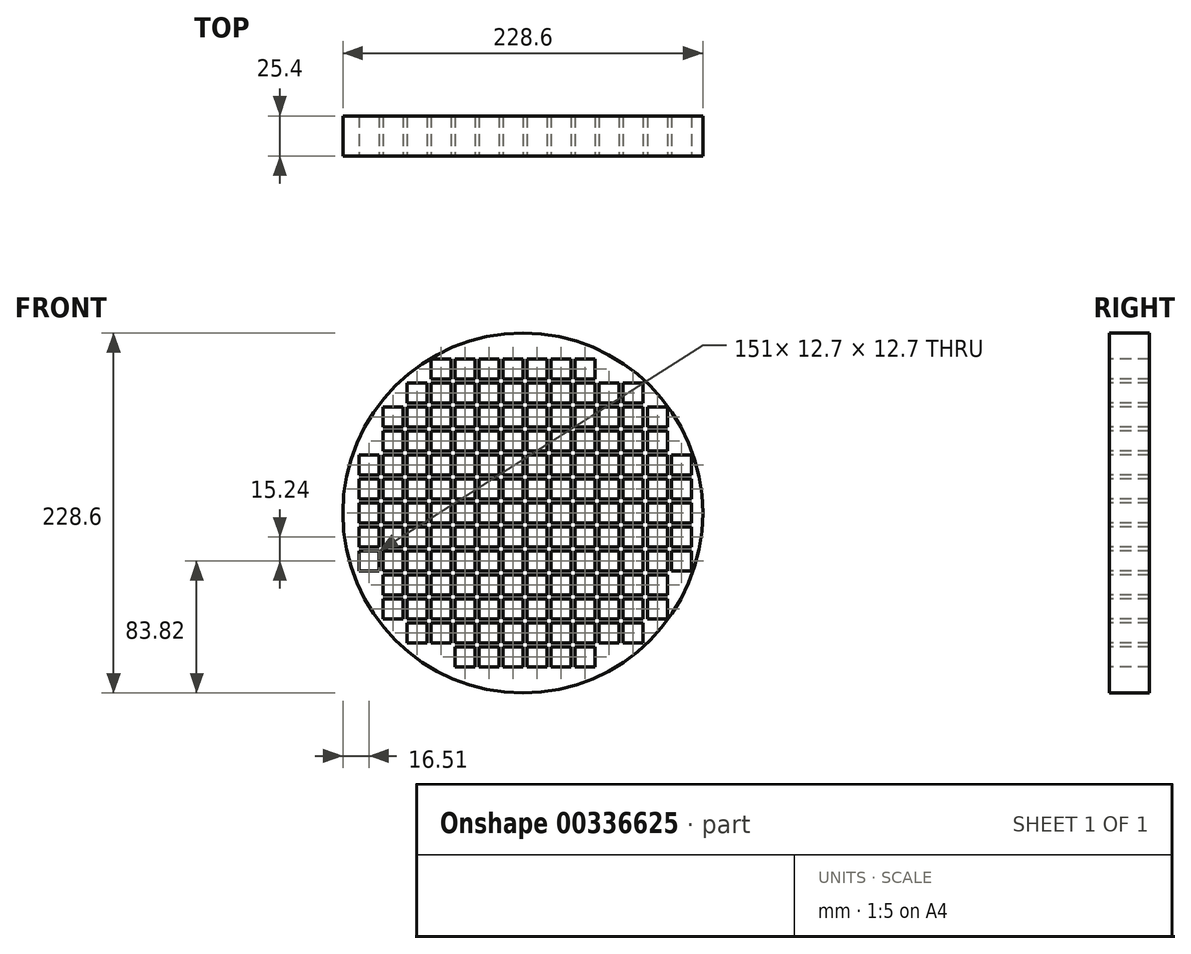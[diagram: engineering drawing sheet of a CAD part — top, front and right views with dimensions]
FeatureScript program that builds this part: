
annotation { "Feature Type Name" : "Feature", "Feature Type Description" : "" }
export const myFeature = defineFeature(function(context is Context, id is Id, definition is map)
    precondition{}
    {
        {
            var Q0;
            Q0=qCreatedBy(makeId("Front.planeOp"),FACE);
            var sketch = newSketch(context, id + "F0", { "sketchPlane" : qUnion([Q0])});
            skCircle(sketch, "E0", {"center": v(0, 0) * mm, "radius": 114.3 * mm});
            skSolve(sketch);
        }
        {
            var Q0;
            Q0 = qSketchRegion(id + "F0", true);
            extrude(context, id + "F1", {"entities" : qUnion([Q0]), "depth" : 25.4 * mm});
        }
        {
            var Q0;
            Q0=makeQuery(id+"F1.opExtrude","CAP_FACE",FACE,{"disambiguationData":[OSD([sQuery(id+"F0.wireOp",EDGE,"E0")])],"isStart":false});
            var sketch = newSketch(context, id + "F2", { "sketchPlane" : qUnion([Q0])});
            skLineSegment(sketch, "E1.bottom", {"start": v(-73.66, 82.55) * mm, "end": v(-60.96, 82.55) * mm});
            skLineSegment(sketch, "E1.top", {"start": v(-73.66, 69.85) * mm, "end": v(-60.96, 69.85) * mm});
            skLineSegment(sketch, "E1.left", {"start": v(-73.66, 82.55) * mm, "end": v(-73.66, 69.85) * mm});
            skLineSegment(sketch, "E1.right", {"start": v(-60.96, 82.55) * mm, "end": v(-60.96, 69.85) * mm});
            skLineSegment(sketch, "E2.0.1.0", {"start": v(-73.66, 67.31) * mm, "end": v(-60.96, 67.31) * mm});
            skLineSegment(sketch, "E2.0.1.1", {"start": v(-73.66, 67.31) * mm, "end": v(-73.66, 54.61) * mm});
            skLineSegment(sketch, "E2.0.1.2", {"start": v(-73.66, 54.61) * mm, "end": v(-60.96, 54.61) * mm});
            skLineSegment(sketch, "E2.0.1.3", {"start": v(-60.96, 67.31) * mm, "end": v(-60.96, 54.61) * mm});
            skLineSegment(sketch, "E2.0.2.0", {"start": v(-73.66, 52.07) * mm, "end": v(-60.96, 52.07) * mm});
            skLineSegment(sketch, "E2.0.2.1", {"start": v(-73.66, 52.07) * mm, "end": v(-73.66, 39.37) * mm});
            skLineSegment(sketch, "E2.0.2.2", {"start": v(-73.66, 39.37) * mm, "end": v(-60.96, 39.37) * mm});
            skLineSegment(sketch, "E2.0.2.3", {"start": v(-60.96, 52.07) * mm, "end": v(-60.96, 39.37) * mm});
            skLineSegment(sketch, "E2.0.3.0", {"start": v(-73.66, 36.83) * mm, "end": v(-60.96, 36.83) * mm});
            skLineSegment(sketch, "E2.0.3.1", {"start": v(-73.66, 36.83) * mm, "end": v(-73.66, 24.13) * mm});
            skLineSegment(sketch, "E2.0.3.2", {"start": v(-73.66, 24.13) * mm, "end": v(-60.96, 24.13) * mm});
            skLineSegment(sketch, "E2.0.3.3", {"start": v(-60.96, 36.83) * mm, "end": v(-60.96, 24.13) * mm});
            skLineSegment(sketch, "E2.0.4.0", {"start": v(-73.66, 21.59) * mm, "end": v(-60.96, 21.59) * mm});
            skLineSegment(sketch, "E2.0.4.1", {"start": v(-73.66, 21.59) * mm, "end": v(-73.66, 8.89) * mm});
            skLineSegment(sketch, "E2.0.4.2", {"start": v(-73.66, 8.89) * mm, "end": v(-60.96, 8.89) * mm});
            skLineSegment(sketch, "E2.0.4.3", {"start": v(-60.96, 21.59) * mm, "end": v(-60.96, 8.89) * mm});
            skLineSegment(sketch, "E2.0.5.0", {"start": v(-73.66, 6.35) * mm, "end": v(-60.96, 6.35) * mm});
            skLineSegment(sketch, "E2.0.5.1", {"start": v(-73.66, 6.35) * mm, "end": v(-73.66, -6.35) * mm});
            skLineSegment(sketch, "E2.0.5.2", {"start": v(-73.66, -6.35) * mm, "end": v(-60.96, -6.35) * mm});
            skLineSegment(sketch, "E2.0.5.3", {"start": v(-60.96, 6.35) * mm, "end": v(-60.96, -6.35) * mm});
            skLineSegment(sketch, "E2.0.6.0", {"start": v(-73.66, -8.9) * mm, "end": v(-60.96, -8.9) * mm});
            skLineSegment(sketch, "E2.0.6.1", {"start": v(-73.66, -8.9) * mm, "end": v(-73.66, -21.6) * mm});
            skLineSegment(sketch, "E2.0.6.2", {"start": v(-73.66, -21.6) * mm, "end": v(-60.96, -21.6) * mm});
            skLineSegment(sketch, "E2.0.6.3", {"start": v(-60.96, -8.9) * mm, "end": v(-60.96, -21.6) * mm});
            skLineSegment(sketch, "E2.0.7.0", {"start": v(-73.66, -24.13) * mm, "end": v(-60.96, -24.13) * mm});
            skLineSegment(sketch, "E2.0.7.1", {"start": v(-73.66, -24.13) * mm, "end": v(-73.66, -36.83) * mm});
            skLineSegment(sketch, "E2.0.7.2", {"start": v(-73.66, -36.83) * mm, "end": v(-60.96, -36.83) * mm});
            skLineSegment(sketch, "E2.0.7.3", {"start": v(-60.96, -24.13) * mm, "end": v(-60.96, -36.83) * mm});
            skLineSegment(sketch, "E2.0.8.0", {"start": v(-73.66, -39.37) * mm, "end": v(-60.96, -39.37) * mm});
            skLineSegment(sketch, "E2.0.8.1", {"start": v(-73.66, -39.37) * mm, "end": v(-73.66, -52.07) * mm});
            skLineSegment(sketch, "E2.0.8.2", {"start": v(-73.66, -52.07) * mm, "end": v(-60.96, -52.07) * mm});
            skLineSegment(sketch, "E2.0.8.3", {"start": v(-60.96, -39.37) * mm, "end": v(-60.96, -52.07) * mm});
            skLineSegment(sketch, "E2.0.9.0", {"start": v(-73.66, -54.61) * mm, "end": v(-60.96, -54.61) * mm});
            skLineSegment(sketch, "E2.0.9.1", {"start": v(-73.66, -54.61) * mm, "end": v(-73.66, -67.31) * mm});
            skLineSegment(sketch, "E2.0.9.2", {"start": v(-73.66, -67.31) * mm, "end": v(-60.96, -67.31) * mm});
            skLineSegment(sketch, "E2.0.9.3", {"start": v(-60.96, -54.61) * mm, "end": v(-60.96, -67.31) * mm});
            skLineSegment(sketch, "E2.1.0.0", {"start": v(-58.42, 82.55) * mm, "end": v(-45.72, 82.55) * mm});
            skLineSegment(sketch, "E2.1.0.1", {"start": v(-58.42, 82.55) * mm, "end": v(-58.42, 69.85) * mm});
            skLineSegment(sketch, "E2.1.0.2", {"start": v(-58.42, 69.85) * mm, "end": v(-45.72, 69.85) * mm});
            skLineSegment(sketch, "E2.1.0.3", {"start": v(-45.72, 82.55) * mm, "end": v(-45.72, 69.85) * mm});
            skLineSegment(sketch, "E2.1.1.0", {"start": v(-58.42, 67.31) * mm, "end": v(-45.72, 67.31) * mm});
            skLineSegment(sketch, "E2.1.1.1", {"start": v(-58.42, 67.31) * mm, "end": v(-58.42, 54.61) * mm});
            skLineSegment(sketch, "E2.1.1.2", {"start": v(-58.42, 54.61) * mm, "end": v(-45.72, 54.61) * mm});
            skLineSegment(sketch, "E2.1.1.3", {"start": v(-45.72, 67.31) * mm, "end": v(-45.72, 54.61) * mm});
            skLineSegment(sketch, "E2.1.2.0", {"start": v(-58.42, 52.07) * mm, "end": v(-45.72, 52.07) * mm});
            skLineSegment(sketch, "E2.1.2.1", {"start": v(-58.42, 52.07) * mm, "end": v(-58.42, 39.37) * mm});
            skLineSegment(sketch, "E2.1.2.2", {"start": v(-58.42, 39.37) * mm, "end": v(-45.72, 39.37) * mm});
            skLineSegment(sketch, "E2.1.2.3", {"start": v(-45.72, 52.07) * mm, "end": v(-45.72, 39.37) * mm});
            skLineSegment(sketch, "E2.1.3.0", {"start": v(-58.42, 36.83) * mm, "end": v(-45.72, 36.83) * mm});
            skLineSegment(sketch, "E2.1.3.1", {"start": v(-58.42, 36.83) * mm, "end": v(-58.42, 24.13) * mm});
            skLineSegment(sketch, "E2.1.3.2", {"start": v(-58.42, 24.13) * mm, "end": v(-45.72, 24.13) * mm});
            skLineSegment(sketch, "E2.1.3.3", {"start": v(-45.72, 36.83) * mm, "end": v(-45.72, 24.13) * mm});
            skLineSegment(sketch, "E2.1.4.0", {"start": v(-58.42, 21.59) * mm, "end": v(-45.72, 21.59) * mm});
            skLineSegment(sketch, "E2.1.4.1", {"start": v(-58.42, 21.59) * mm, "end": v(-58.42, 8.89) * mm});
            skLineSegment(sketch, "E2.1.4.2", {"start": v(-58.42, 8.89) * mm, "end": v(-45.72, 8.89) * mm});
            skLineSegment(sketch, "E2.1.4.3", {"start": v(-45.72, 21.59) * mm, "end": v(-45.72, 8.89) * mm});
            skLineSegment(sketch, "E2.1.5.0", {"start": v(-58.42, 6.35) * mm, "end": v(-45.72, 6.35) * mm});
            skLineSegment(sketch, "E2.1.5.1", {"start": v(-58.42, 6.35) * mm, "end": v(-58.42, -6.35) * mm});
            skLineSegment(sketch, "E2.1.5.2", {"start": v(-58.42, -6.35) * mm, "end": v(-45.72, -6.35) * mm});
            skLineSegment(sketch, "E2.1.5.3", {"start": v(-45.72, 6.35) * mm, "end": v(-45.72, -6.35) * mm});
            skLineSegment(sketch, "E2.1.6.0", {"start": v(-58.42, -8.9) * mm, "end": v(-45.72, -8.9) * mm});
            skLineSegment(sketch, "E2.1.6.1", {"start": v(-58.42, -8.9) * mm, "end": v(-58.42, -21.6) * mm});
            skLineSegment(sketch, "E2.1.6.2", {"start": v(-58.42, -21.6) * mm, "end": v(-45.72, -21.6) * mm});
            skLineSegment(sketch, "E2.1.6.3", {"start": v(-45.72, -8.9) * mm, "end": v(-45.72, -21.6) * mm});
            skLineSegment(sketch, "E2.1.7.0", {"start": v(-58.42, -24.13) * mm, "end": v(-45.72, -24.13) * mm});
            skLineSegment(sketch, "E2.1.7.1", {"start": v(-58.42, -24.13) * mm, "end": v(-58.42, -36.83) * mm});
            skLineSegment(sketch, "E2.1.7.2", {"start": v(-58.42, -36.83) * mm, "end": v(-45.72, -36.83) * mm});
            skLineSegment(sketch, "E2.1.7.3", {"start": v(-45.72, -24.13) * mm, "end": v(-45.72, -36.83) * mm});
            skLineSegment(sketch, "E2.1.8.0", {"start": v(-58.42, -39.37) * mm, "end": v(-45.72, -39.37) * mm});
            skLineSegment(sketch, "E2.1.8.1", {"start": v(-58.42, -39.37) * mm, "end": v(-58.42, -52.07) * mm});
            skLineSegment(sketch, "E2.1.8.2", {"start": v(-58.42, -52.07) * mm, "end": v(-45.72, -52.07) * mm});
            skLineSegment(sketch, "E2.1.8.3", {"start": v(-45.72, -39.37) * mm, "end": v(-45.72, -52.07) * mm});
            skLineSegment(sketch, "E2.1.9.0", {"start": v(-58.42, -54.61) * mm, "end": v(-45.72, -54.61) * mm});
            skLineSegment(sketch, "E2.1.9.1", {"start": v(-58.42, -54.61) * mm, "end": v(-58.42, -67.31) * mm});
            skLineSegment(sketch, "E2.1.9.2", {"start": v(-58.42, -67.31) * mm, "end": v(-45.72, -67.31) * mm});
            skLineSegment(sketch, "E2.1.9.3", {"start": v(-45.72, -54.61) * mm, "end": v(-45.72, -67.31) * mm});
            skLineSegment(sketch, "E2.2.0.0", {"start": v(-43.18, 82.55) * mm, "end": v(-30.48, 82.55) * mm});
            skLineSegment(sketch, "E2.2.0.1", {"start": v(-43.18, 82.55) * mm, "end": v(-43.18, 69.85) * mm});
            skLineSegment(sketch, "E2.2.0.2", {"start": v(-43.18, 69.85) * mm, "end": v(-30.48, 69.85) * mm});
            skLineSegment(sketch, "E2.2.0.3", {"start": v(-30.48, 82.55) * mm, "end": v(-30.48, 69.85) * mm});
            skLineSegment(sketch, "E2.2.1.0", {"start": v(-43.18, 67.31) * mm, "end": v(-30.48, 67.31) * mm});
            skLineSegment(sketch, "E2.2.1.1", {"start": v(-43.18, 67.31) * mm, "end": v(-43.18, 54.61) * mm});
            skLineSegment(sketch, "E2.2.1.2", {"start": v(-43.18, 54.61) * mm, "end": v(-30.48, 54.61) * mm});
            skLineSegment(sketch, "E2.2.1.3", {"start": v(-30.48, 67.31) * mm, "end": v(-30.48, 54.61) * mm});
            skLineSegment(sketch, "E2.2.2.0", {"start": v(-43.18, 52.07) * mm, "end": v(-30.48, 52.07) * mm});
            skLineSegment(sketch, "E2.2.2.1", {"start": v(-43.18, 52.07) * mm, "end": v(-43.18, 39.37) * mm});
            skLineSegment(sketch, "E2.2.2.2", {"start": v(-43.18, 39.37) * mm, "end": v(-30.48, 39.37) * mm});
            skLineSegment(sketch, "E2.2.2.3", {"start": v(-30.48, 52.07) * mm, "end": v(-30.48, 39.37) * mm});
            skLineSegment(sketch, "E2.2.3.0", {"start": v(-43.18, 36.83) * mm, "end": v(-30.48, 36.83) * mm});
            skLineSegment(sketch, "E2.2.3.1", {"start": v(-43.18, 36.83) * mm, "end": v(-43.18, 24.13) * mm});
            skLineSegment(sketch, "E2.2.3.2", {"start": v(-43.18, 24.13) * mm, "end": v(-30.48, 24.13) * mm});
            skLineSegment(sketch, "E2.2.3.3", {"start": v(-30.48, 36.83) * mm, "end": v(-30.48, 24.13) * mm});
            skLineSegment(sketch, "E2.2.4.0", {"start": v(-43.18, 21.59) * mm, "end": v(-30.48, 21.59) * mm});
            skLineSegment(sketch, "E2.2.4.1", {"start": v(-43.18, 21.59) * mm, "end": v(-43.18, 8.89) * mm});
            skLineSegment(sketch, "E2.2.4.2", {"start": v(-43.18, 8.89) * mm, "end": v(-30.48, 8.89) * mm});
            skLineSegment(sketch, "E2.2.4.3", {"start": v(-30.48, 21.59) * mm, "end": v(-30.48, 8.89) * mm});
            skLineSegment(sketch, "E2.2.5.0", {"start": v(-43.18, 6.35) * mm, "end": v(-30.48, 6.35) * mm});
            skLineSegment(sketch, "E2.2.5.1", {"start": v(-43.18, 6.35) * mm, "end": v(-43.18, -6.35) * mm});
            skLineSegment(sketch, "E2.2.5.2", {"start": v(-43.18, -6.35) * mm, "end": v(-30.48, -6.35) * mm});
            skLineSegment(sketch, "E2.2.5.3", {"start": v(-30.48, 6.35) * mm, "end": v(-30.48, -6.35) * mm});
            skLineSegment(sketch, "E2.2.6.0", {"start": v(-43.18, -8.9) * mm, "end": v(-30.48, -8.9) * mm});
            skLineSegment(sketch, "E2.2.6.1", {"start": v(-43.18, -8.9) * mm, "end": v(-43.18, -21.6) * mm});
            skLineSegment(sketch, "E2.2.6.2", {"start": v(-43.18, -21.6) * mm, "end": v(-30.48, -21.6) * mm});
            skLineSegment(sketch, "E2.2.6.3", {"start": v(-30.48, -8.9) * mm, "end": v(-30.48, -21.6) * mm});
            skLineSegment(sketch, "E2.2.7.0", {"start": v(-43.18, -24.13) * mm, "end": v(-30.48, -24.13) * mm});
            skLineSegment(sketch, "E2.2.7.1", {"start": v(-43.18, -24.13) * mm, "end": v(-43.18, -36.83) * mm});
            skLineSegment(sketch, "E2.2.7.2", {"start": v(-43.18, -36.83) * mm, "end": v(-30.48, -36.83) * mm});
            skLineSegment(sketch, "E2.2.7.3", {"start": v(-30.48, -24.13) * mm, "end": v(-30.48, -36.83) * mm});
            skLineSegment(sketch, "E2.2.8.0", {"start": v(-43.18, -39.37) * mm, "end": v(-30.48, -39.37) * mm});
            skLineSegment(sketch, "E2.2.8.1", {"start": v(-43.18, -39.37) * mm, "end": v(-43.18, -52.07) * mm});
            skLineSegment(sketch, "E2.2.8.2", {"start": v(-43.18, -52.07) * mm, "end": v(-30.48, -52.07) * mm});
            skLineSegment(sketch, "E2.2.8.3", {"start": v(-30.48, -39.37) * mm, "end": v(-30.48, -52.07) * mm});
            skLineSegment(sketch, "E2.2.9.0", {"start": v(-43.18, -54.61) * mm, "end": v(-30.48, -54.61) * mm});
            skLineSegment(sketch, "E2.2.9.1", {"start": v(-43.18, -54.61) * mm, "end": v(-43.18, -67.31) * mm});
            skLineSegment(sketch, "E2.2.9.2", {"start": v(-43.18, -67.31) * mm, "end": v(-30.48, -67.31) * mm});
            skLineSegment(sketch, "E2.2.9.3", {"start": v(-30.48, -54.61) * mm, "end": v(-30.48, -67.31) * mm});
            skLineSegment(sketch, "E2.3.0.0", {"start": v(-27.94, 82.55) * mm, "end": v(-15.24, 82.55) * mm});
            skLineSegment(sketch, "E2.3.0.1", {"start": v(-27.94, 82.55) * mm, "end": v(-27.94, 69.85) * mm});
            skLineSegment(sketch, "E2.3.0.2", {"start": v(-27.94, 69.85) * mm, "end": v(-15.24, 69.85) * mm});
            skLineSegment(sketch, "E2.3.0.3", {"start": v(-15.24, 82.55) * mm, "end": v(-15.24, 69.85) * mm});
            skLineSegment(sketch, "E2.3.1.0", {"start": v(-27.94, 67.31) * mm, "end": v(-15.24, 67.31) * mm});
            skLineSegment(sketch, "E2.3.1.1", {"start": v(-27.94, 67.31) * mm, "end": v(-27.94, 54.61) * mm});
            skLineSegment(sketch, "E2.3.1.2", {"start": v(-27.94, 54.61) * mm, "end": v(-15.24, 54.61) * mm});
            skLineSegment(sketch, "E2.3.1.3", {"start": v(-15.24, 67.31) * mm, "end": v(-15.24, 54.61) * mm});
            skLineSegment(sketch, "E2.3.2.0", {"start": v(-27.94, 52.07) * mm, "end": v(-15.24, 52.07) * mm});
            skLineSegment(sketch, "E2.3.2.1", {"start": v(-27.94, 52.07) * mm, "end": v(-27.94, 39.37) * mm});
            skLineSegment(sketch, "E2.3.2.2", {"start": v(-27.94, 39.37) * mm, "end": v(-15.24, 39.37) * mm});
            skLineSegment(sketch, "E2.3.2.3", {"start": v(-15.24, 52.07) * mm, "end": v(-15.24, 39.37) * mm});
            skLineSegment(sketch, "E2.3.3.0", {"start": v(-27.94, 36.83) * mm, "end": v(-15.24, 36.83) * mm});
            skLineSegment(sketch, "E2.3.3.1", {"start": v(-27.94, 36.83) * mm, "end": v(-27.94, 24.13) * mm});
            skLineSegment(sketch, "E2.3.3.2", {"start": v(-27.94, 24.13) * mm, "end": v(-15.24, 24.13) * mm});
            skLineSegment(sketch, "E2.3.3.3", {"start": v(-15.24, 36.83) * mm, "end": v(-15.24, 24.13) * mm});
            skLineSegment(sketch, "E2.3.4.0", {"start": v(-27.94, 21.59) * mm, "end": v(-15.24, 21.59) * mm});
            skLineSegment(sketch, "E2.3.4.1", {"start": v(-27.94, 21.59) * mm, "end": v(-27.94, 8.89) * mm});
            skLineSegment(sketch, "E2.3.4.2", {"start": v(-27.94, 8.89) * mm, "end": v(-15.24, 8.89) * mm});
            skLineSegment(sketch, "E2.3.4.3", {"start": v(-15.24, 21.59) * mm, "end": v(-15.24, 8.89) * mm});
            skLineSegment(sketch, "E2.3.5.0", {"start": v(-27.94, 6.35) * mm, "end": v(-15.24, 6.35) * mm});
            skLineSegment(sketch, "E2.3.5.1", {"start": v(-27.94, 6.35) * mm, "end": v(-27.94, -6.35) * mm});
            skLineSegment(sketch, "E2.3.5.2", {"start": v(-27.94, -6.35) * mm, "end": v(-15.24, -6.35) * mm});
            skLineSegment(sketch, "E2.3.5.3", {"start": v(-15.24, 6.35) * mm, "end": v(-15.24, -6.35) * mm});
            skLineSegment(sketch, "E2.3.6.0", {"start": v(-27.94, -8.9) * mm, "end": v(-15.24, -8.9) * mm});
            skLineSegment(sketch, "E2.3.6.1", {"start": v(-27.94, -8.9) * mm, "end": v(-27.94, -21.6) * mm});
            skLineSegment(sketch, "E2.3.6.2", {"start": v(-27.94, -21.6) * mm, "end": v(-15.24, -21.6) * mm});
            skLineSegment(sketch, "E2.3.6.3", {"start": v(-15.24, -8.9) * mm, "end": v(-15.24, -21.6) * mm});
            skLineSegment(sketch, "E2.3.7.0", {"start": v(-27.94, -24.13) * mm, "end": v(-15.24, -24.13) * mm});
            skLineSegment(sketch, "E2.3.7.1", {"start": v(-27.94, -24.13) * mm, "end": v(-27.94, -36.83) * mm});
            skLineSegment(sketch, "E2.3.7.2", {"start": v(-27.94, -36.83) * mm, "end": v(-15.24, -36.83) * mm});
            skLineSegment(sketch, "E2.3.7.3", {"start": v(-15.24, -24.13) * mm, "end": v(-15.24, -36.83) * mm});
            skLineSegment(sketch, "E2.3.8.0", {"start": v(-27.94, -39.37) * mm, "end": v(-15.24, -39.37) * mm});
            skLineSegment(sketch, "E2.3.8.1", {"start": v(-27.94, -39.37) * mm, "end": v(-27.94, -52.07) * mm});
            skLineSegment(sketch, "E2.3.8.2", {"start": v(-27.94, -52.07) * mm, "end": v(-15.24, -52.07) * mm});
            skLineSegment(sketch, "E2.3.8.3", {"start": v(-15.24, -39.37) * mm, "end": v(-15.24, -52.07) * mm});
            skLineSegment(sketch, "E2.3.9.0", {"start": v(-27.94, -54.61) * mm, "end": v(-15.24, -54.61) * mm});
            skLineSegment(sketch, "E2.3.9.1", {"start": v(-27.94, -54.61) * mm, "end": v(-27.94, -67.31) * mm});
            skLineSegment(sketch, "E2.3.9.2", {"start": v(-27.94, -67.31) * mm, "end": v(-15.24, -67.31) * mm});
            skLineSegment(sketch, "E2.3.9.3", {"start": v(-15.24, -54.61) * mm, "end": v(-15.24, -67.31) * mm});
            skLineSegment(sketch, "E2.4.0.0", {"start": v(-12.7, 82.55) * mm, "end": v(0, 82.55) * mm});
            skLineSegment(sketch, "E2.4.0.1", {"start": v(-12.7, 82.55) * mm, "end": v(-12.7, 69.85) * mm});
            skLineSegment(sketch, "E2.4.0.2", {"start": v(-12.7, 69.85) * mm, "end": v(0, 69.85) * mm});
            skLineSegment(sketch, "E2.4.0.3", {"start": v(0, 82.55) * mm, "end": v(0, 69.85) * mm});
            skLineSegment(sketch, "E2.4.1.0", {"start": v(-12.7, 67.31) * mm, "end": v(0, 67.31) * mm});
            skLineSegment(sketch, "E2.4.1.1", {"start": v(-12.7, 67.31) * mm, "end": v(-12.7, 54.61) * mm});
            skLineSegment(sketch, "E2.4.1.2", {"start": v(-12.7, 54.61) * mm, "end": v(0, 54.61) * mm});
            skLineSegment(sketch, "E2.4.1.3", {"start": v(0, 67.31) * mm, "end": v(0, 54.61) * mm});
            skLineSegment(sketch, "E2.4.2.0", {"start": v(-12.7, 52.07) * mm, "end": v(0, 52.07) * mm});
            skLineSegment(sketch, "E2.4.2.1", {"start": v(-12.7, 52.07) * mm, "end": v(-12.7, 39.37) * mm});
            skLineSegment(sketch, "E2.4.2.2", {"start": v(-12.7, 39.37) * mm, "end": v(0, 39.37) * mm});
            skLineSegment(sketch, "E2.4.2.3", {"start": v(0, 52.07) * mm, "end": v(0, 39.37) * mm});
            skLineSegment(sketch, "E2.4.3.0", {"start": v(-12.7, 36.83) * mm, "end": v(0, 36.83) * mm});
            skLineSegment(sketch, "E2.4.3.1", {"start": v(-12.7, 36.83) * mm, "end": v(-12.7, 24.13) * mm});
            skLineSegment(sketch, "E2.4.3.2", {"start": v(-12.7, 24.13) * mm, "end": v(0, 24.13) * mm});
            skLineSegment(sketch, "E2.4.3.3", {"start": v(0, 36.83) * mm, "end": v(0, 24.13) * mm});
            skLineSegment(sketch, "E2.4.4.0", {"start": v(-12.7, 21.59) * mm, "end": v(0, 21.59) * mm});
            skLineSegment(sketch, "E2.4.4.1", {"start": v(-12.7, 21.59) * mm, "end": v(-12.7, 8.89) * mm});
            skLineSegment(sketch, "E2.4.4.2", {"start": v(-12.7, 8.89) * mm, "end": v(0, 8.89) * mm});
            skLineSegment(sketch, "E2.4.4.3", {"start": v(0, 21.59) * mm, "end": v(0, 8.89) * mm});
            skLineSegment(sketch, "E2.4.5.0", {"start": v(-12.7, 6.35) * mm, "end": v(0, 6.35) * mm});
            skLineSegment(sketch, "E2.4.5.1", {"start": v(-12.7, 6.35) * mm, "end": v(-12.7, -6.35) * mm});
            skLineSegment(sketch, "E2.4.5.2", {"start": v(-12.7, -6.35) * mm, "end": v(0, -6.35) * mm});
            skLineSegment(sketch, "E2.4.5.3", {"start": v(0, 6.35) * mm, "end": v(0, -6.35) * mm});
            skLineSegment(sketch, "E2.4.6.0", {"start": v(-12.7, -8.9) * mm, "end": v(0, -8.9) * mm});
            skLineSegment(sketch, "E2.4.6.1", {"start": v(-12.7, -8.9) * mm, "end": v(-12.7, -21.6) * mm});
            skLineSegment(sketch, "E2.4.6.2", {"start": v(-12.7, -21.6) * mm, "end": v(0, -21.6) * mm});
            skLineSegment(sketch, "E2.4.6.3", {"start": v(0, -8.9) * mm, "end": v(0, -21.6) * mm});
            skLineSegment(sketch, "E2.4.7.0", {"start": v(-12.7, -24.13) * mm, "end": v(0, -24.13) * mm});
            skLineSegment(sketch, "E2.4.7.1", {"start": v(-12.7, -24.13) * mm, "end": v(-12.7, -36.83) * mm});
            skLineSegment(sketch, "E2.4.7.2", {"start": v(-12.7, -36.83) * mm, "end": v(0, -36.83) * mm});
            skLineSegment(sketch, "E2.4.7.3", {"start": v(0, -24.13) * mm, "end": v(0, -36.83) * mm});
            skLineSegment(sketch, "E2.4.8.0", {"start": v(-12.7, -39.37) * mm, "end": v(0, -39.37) * mm});
            skLineSegment(sketch, "E2.4.8.1", {"start": v(-12.7, -39.37) * mm, "end": v(-12.7, -52.07) * mm});
            skLineSegment(sketch, "E2.4.8.2", {"start": v(-12.7, -52.07) * mm, "end": v(0, -52.07) * mm});
            skLineSegment(sketch, "E2.4.8.3", {"start": v(0, -39.37) * mm, "end": v(0, -52.07) * mm});
            skLineSegment(sketch, "E2.4.9.0", {"start": v(-12.7, -54.61) * mm, "end": v(0, -54.61) * mm});
            skLineSegment(sketch, "E2.4.9.1", {"start": v(-12.7, -54.61) * mm, "end": v(-12.7, -67.31) * mm});
            skLineSegment(sketch, "E2.4.9.2", {"start": v(-12.7, -67.31) * mm, "end": v(0, -67.31) * mm});
            skLineSegment(sketch, "E2.4.9.3", {"start": v(0, -54.61) * mm, "end": v(0, -67.31) * mm});
            skLineSegment(sketch, "E2.5.0.0", {"start": v(2.54, 82.55) * mm, "end": v(15.24, 82.55) * mm});
            skLineSegment(sketch, "E2.5.0.1", {"start": v(2.54, 82.55) * mm, "end": v(2.54, 69.85) * mm});
            skLineSegment(sketch, "E2.5.0.2", {"start": v(2.54, 69.85) * mm, "end": v(15.24, 69.85) * mm});
            skLineSegment(sketch, "E2.5.0.3", {"start": v(15.24, 82.55) * mm, "end": v(15.24, 69.85) * mm});
            skLineSegment(sketch, "E2.5.1.0", {"start": v(2.54, 67.31) * mm, "end": v(15.24, 67.31) * mm});
            skLineSegment(sketch, "E2.5.1.1", {"start": v(2.54, 67.31) * mm, "end": v(2.54, 54.61) * mm});
            skLineSegment(sketch, "E2.5.1.2", {"start": v(2.54, 54.61) * mm, "end": v(15.24, 54.61) * mm});
            skLineSegment(sketch, "E2.5.1.3", {"start": v(15.24, 67.31) * mm, "end": v(15.24, 54.61) * mm});
            skLineSegment(sketch, "E2.5.2.0", {"start": v(2.54, 52.07) * mm, "end": v(15.24, 52.07) * mm});
            skLineSegment(sketch, "E2.5.2.1", {"start": v(2.54, 52.07) * mm, "end": v(2.54, 39.37) * mm});
            skLineSegment(sketch, "E2.5.2.2", {"start": v(2.54, 39.37) * mm, "end": v(15.24, 39.37) * mm});
            skLineSegment(sketch, "E2.5.2.3", {"start": v(15.24, 52.07) * mm, "end": v(15.24, 39.37) * mm});
            skLineSegment(sketch, "E2.5.3.0", {"start": v(2.54, 36.83) * mm, "end": v(15.24, 36.83) * mm});
            skLineSegment(sketch, "E2.5.3.1", {"start": v(2.54, 36.83) * mm, "end": v(2.54, 24.13) * mm});
            skLineSegment(sketch, "E2.5.3.2", {"start": v(2.54, 24.13) * mm, "end": v(15.24, 24.13) * mm});
            skLineSegment(sketch, "E2.5.3.3", {"start": v(15.24, 36.83) * mm, "end": v(15.24, 24.13) * mm});
            skLineSegment(sketch, "E2.5.4.0", {"start": v(2.54, 21.59) * mm, "end": v(15.24, 21.59) * mm});
            skLineSegment(sketch, "E2.5.4.1", {"start": v(2.54, 21.59) * mm, "end": v(2.54, 8.89) * mm});
            skLineSegment(sketch, "E2.5.4.2", {"start": v(2.54, 8.89) * mm, "end": v(15.24, 8.89) * mm});
            skLineSegment(sketch, "E2.5.4.3", {"start": v(15.24, 21.59) * mm, "end": v(15.24, 8.89) * mm});
            skLineSegment(sketch, "E2.5.5.0", {"start": v(2.54, 6.35) * mm, "end": v(15.24, 6.35) * mm});
            skLineSegment(sketch, "E2.5.5.1", {"start": v(2.54, 6.35) * mm, "end": v(2.54, -6.35) * mm});
            skLineSegment(sketch, "E2.5.5.2", {"start": v(2.54, -6.35) * mm, "end": v(15.24, -6.35) * mm});
            skLineSegment(sketch, "E2.5.5.3", {"start": v(15.24, 6.35) * mm, "end": v(15.24, -6.35) * mm});
            skLineSegment(sketch, "E2.5.6.0", {"start": v(2.54, -8.9) * mm, "end": v(15.24, -8.9) * mm});
            skLineSegment(sketch, "E2.5.6.1", {"start": v(2.54, -8.9) * mm, "end": v(2.54, -21.6) * mm});
            skLineSegment(sketch, "E2.5.6.2", {"start": v(2.54, -21.6) * mm, "end": v(15.24, -21.6) * mm});
            skLineSegment(sketch, "E2.5.6.3", {"start": v(15.24, -8.9) * mm, "end": v(15.24, -21.6) * mm});
            skLineSegment(sketch, "E2.5.7.0", {"start": v(2.54, -24.13) * mm, "end": v(15.24, -24.13) * mm});
            skLineSegment(sketch, "E2.5.7.1", {"start": v(2.54, -24.13) * mm, "end": v(2.54, -36.83) * mm});
            skLineSegment(sketch, "E2.5.7.2", {"start": v(2.54, -36.83) * mm, "end": v(15.24, -36.83) * mm});
            skLineSegment(sketch, "E2.5.7.3", {"start": v(15.24, -24.13) * mm, "end": v(15.24, -36.83) * mm});
            skLineSegment(sketch, "E2.5.8.0", {"start": v(2.54, -39.37) * mm, "end": v(15.24, -39.37) * mm});
            skLineSegment(sketch, "E2.5.8.1", {"start": v(2.54, -39.37) * mm, "end": v(2.54, -52.07) * mm});
            skLineSegment(sketch, "E2.5.8.2", {"start": v(2.54, -52.07) * mm, "end": v(15.24, -52.07) * mm});
            skLineSegment(sketch, "E2.5.8.3", {"start": v(15.24, -39.37) * mm, "end": v(15.24, -52.07) * mm});
            skLineSegment(sketch, "E2.5.9.0", {"start": v(2.54, -54.61) * mm, "end": v(15.24, -54.61) * mm});
            skLineSegment(sketch, "E2.5.9.1", {"start": v(2.54, -54.61) * mm, "end": v(2.54, -67.31) * mm});
            skLineSegment(sketch, "E2.5.9.2", {"start": v(2.54, -67.31) * mm, "end": v(15.24, -67.31) * mm});
            skLineSegment(sketch, "E2.5.9.3", {"start": v(15.24, -54.61) * mm, "end": v(15.24, -67.31) * mm});
            skLineSegment(sketch, "E2.6.0.0", {"start": v(17.78, 82.55) * mm, "end": v(30.48, 82.55) * mm});
            skLineSegment(sketch, "E2.6.0.1", {"start": v(17.78, 82.55) * mm, "end": v(17.78, 69.85) * mm});
            skLineSegment(sketch, "E2.6.0.2", {"start": v(17.78, 69.85) * mm, "end": v(30.48, 69.85) * mm});
            skLineSegment(sketch, "E2.6.0.3", {"start": v(30.48, 82.55) * mm, "end": v(30.48, 69.85) * mm});
            skLineSegment(sketch, "E2.6.1.0", {"start": v(17.78, 67.31) * mm, "end": v(30.48, 67.31) * mm});
            skLineSegment(sketch, "E2.6.1.1", {"start": v(17.78, 67.31) * mm, "end": v(17.78, 54.61) * mm});
            skLineSegment(sketch, "E2.6.1.2", {"start": v(17.78, 54.61) * mm, "end": v(30.48, 54.61) * mm});
            skLineSegment(sketch, "E2.6.1.3", {"start": v(30.48, 67.31) * mm, "end": v(30.48, 54.61) * mm});
            skLineSegment(sketch, "E2.6.2.0", {"start": v(17.78, 52.07) * mm, "end": v(30.48, 52.07) * mm});
            skLineSegment(sketch, "E2.6.2.1", {"start": v(17.78, 52.07) * mm, "end": v(17.78, 39.37) * mm});
            skLineSegment(sketch, "E2.6.2.2", {"start": v(17.78, 39.37) * mm, "end": v(30.48, 39.37) * mm});
            skLineSegment(sketch, "E2.6.2.3", {"start": v(30.48, 52.07) * mm, "end": v(30.48, 39.37) * mm});
            skLineSegment(sketch, "E2.6.3.0", {"start": v(17.78, 36.83) * mm, "end": v(30.48, 36.83) * mm});
            skLineSegment(sketch, "E2.6.3.1", {"start": v(17.78, 36.83) * mm, "end": v(17.78, 24.13) * mm});
            skLineSegment(sketch, "E2.6.3.2", {"start": v(17.78, 24.13) * mm, "end": v(30.48, 24.13) * mm});
            skLineSegment(sketch, "E2.6.3.3", {"start": v(30.48, 36.83) * mm, "end": v(30.48, 24.13) * mm});
            skLineSegment(sketch, "E2.6.4.0", {"start": v(17.78, 21.59) * mm, "end": v(30.48, 21.59) * mm});
            skLineSegment(sketch, "E2.6.4.1", {"start": v(17.78, 21.59) * mm, "end": v(17.78, 8.89) * mm});
            skLineSegment(sketch, "E2.6.4.2", {"start": v(17.78, 8.89) * mm, "end": v(30.48, 8.89) * mm});
            skLineSegment(sketch, "E2.6.4.3", {"start": v(30.48, 21.59) * mm, "end": v(30.48, 8.89) * mm});
            skLineSegment(sketch, "E2.6.5.0", {"start": v(17.78, 6.35) * mm, "end": v(30.48, 6.35) * mm});
            skLineSegment(sketch, "E2.6.5.1", {"start": v(17.78, 6.35) * mm, "end": v(17.78, -6.35) * mm});
            skLineSegment(sketch, "E2.6.5.2", {"start": v(17.78, -6.35) * mm, "end": v(30.48, -6.35) * mm});
            skLineSegment(sketch, "E2.6.5.3", {"start": v(30.48, 6.35) * mm, "end": v(30.48, -6.35) * mm});
            skLineSegment(sketch, "E2.6.6.0", {"start": v(17.78, -8.9) * mm, "end": v(30.48, -8.9) * mm});
            skLineSegment(sketch, "E2.6.6.1", {"start": v(17.78, -8.9) * mm, "end": v(17.78, -21.6) * mm});
            skLineSegment(sketch, "E2.6.6.2", {"start": v(17.78, -21.6) * mm, "end": v(30.48, -21.6) * mm});
            skLineSegment(sketch, "E2.6.6.3", {"start": v(30.48, -8.9) * mm, "end": v(30.48, -21.6) * mm});
            skLineSegment(sketch, "E2.6.7.0", {"start": v(17.78, -24.13) * mm, "end": v(30.48, -24.13) * mm});
            skLineSegment(sketch, "E2.6.7.1", {"start": v(17.78, -24.13) * mm, "end": v(17.78, -36.83) * mm});
            skLineSegment(sketch, "E2.6.7.2", {"start": v(17.78, -36.83) * mm, "end": v(30.48, -36.83) * mm});
            skLineSegment(sketch, "E2.6.7.3", {"start": v(30.48, -24.13) * mm, "end": v(30.48, -36.83) * mm});
            skLineSegment(sketch, "E2.6.8.0", {"start": v(17.78, -39.37) * mm, "end": v(30.48, -39.37) * mm});
            skLineSegment(sketch, "E2.6.8.1", {"start": v(17.78, -39.37) * mm, "end": v(17.78, -52.07) * mm});
            skLineSegment(sketch, "E2.6.8.2", {"start": v(17.78, -52.07) * mm, "end": v(30.48, -52.07) * mm});
            skLineSegment(sketch, "E2.6.8.3", {"start": v(30.48, -39.37) * mm, "end": v(30.48, -52.07) * mm});
            skLineSegment(sketch, "E2.6.9.0", {"start": v(17.78, -54.61) * mm, "end": v(30.48, -54.61) * mm});
            skLineSegment(sketch, "E2.6.9.1", {"start": v(17.78, -54.61) * mm, "end": v(17.78, -67.31) * mm});
            skLineSegment(sketch, "E2.6.9.2", {"start": v(17.78, -67.31) * mm, "end": v(30.48, -67.31) * mm});
            skLineSegment(sketch, "E2.6.9.3", {"start": v(30.48, -54.61) * mm, "end": v(30.48, -67.31) * mm});
            skLineSegment(sketch, "E2.7.0.0", {"start": v(33.02, 82.55) * mm, "end": v(45.72, 82.55) * mm});
            skLineSegment(sketch, "E2.7.0.1", {"start": v(33.02, 82.55) * mm, "end": v(33.02, 69.85) * mm});
            skLineSegment(sketch, "E2.7.0.2", {"start": v(33.02, 69.85) * mm, "end": v(45.72, 69.85) * mm});
            skLineSegment(sketch, "E2.7.0.3", {"start": v(45.72, 82.55) * mm, "end": v(45.72, 69.85) * mm});
            skLineSegment(sketch, "E2.7.1.0", {"start": v(33.02, 67.31) * mm, "end": v(45.72, 67.31) * mm});
            skLineSegment(sketch, "E2.7.1.1", {"start": v(33.02, 67.31) * mm, "end": v(33.02, 54.61) * mm});
            skLineSegment(sketch, "E2.7.1.2", {"start": v(33.02, 54.61) * mm, "end": v(45.72, 54.61) * mm});
            skLineSegment(sketch, "E2.7.1.3", {"start": v(45.72, 67.31) * mm, "end": v(45.72, 54.61) * mm});
            skLineSegment(sketch, "E2.7.2.0", {"start": v(33.02, 52.07) * mm, "end": v(45.72, 52.07) * mm});
            skLineSegment(sketch, "E2.7.2.1", {"start": v(33.02, 52.07) * mm, "end": v(33.02, 39.37) * mm});
            skLineSegment(sketch, "E2.7.2.2", {"start": v(33.02, 39.37) * mm, "end": v(45.72, 39.37) * mm});
            skLineSegment(sketch, "E2.7.2.3", {"start": v(45.72, 52.07) * mm, "end": v(45.72, 39.37) * mm});
            skLineSegment(sketch, "E2.7.3.0", {"start": v(33.02, 36.83) * mm, "end": v(45.72, 36.83) * mm});
            skLineSegment(sketch, "E2.7.3.1", {"start": v(33.02, 36.83) * mm, "end": v(33.02, 24.13) * mm});
            skLineSegment(sketch, "E2.7.3.2", {"start": v(33.02, 24.13) * mm, "end": v(45.72, 24.13) * mm});
            skLineSegment(sketch, "E2.7.3.3", {"start": v(45.72, 36.83) * mm, "end": v(45.72, 24.13) * mm});
            skLineSegment(sketch, "E2.7.4.0", {"start": v(33.02, 21.59) * mm, "end": v(45.72, 21.59) * mm});
            skLineSegment(sketch, "E2.7.4.1", {"start": v(33.02, 21.59) * mm, "end": v(33.02, 8.89) * mm});
            skLineSegment(sketch, "E2.7.4.2", {"start": v(33.02, 8.89) * mm, "end": v(45.72, 8.89) * mm});
            skLineSegment(sketch, "E2.7.4.3", {"start": v(45.72, 21.59) * mm, "end": v(45.72, 8.89) * mm});
            skLineSegment(sketch, "E2.7.5.0", {"start": v(33.02, 6.35) * mm, "end": v(45.72, 6.35) * mm});
            skLineSegment(sketch, "E2.7.5.1", {"start": v(33.02, 6.35) * mm, "end": v(33.02, -6.35) * mm});
            skLineSegment(sketch, "E2.7.5.2", {"start": v(33.02, -6.35) * mm, "end": v(45.72, -6.35) * mm});
            skLineSegment(sketch, "E2.7.5.3", {"start": v(45.72, 6.35) * mm, "end": v(45.72, -6.35) * mm});
            skLineSegment(sketch, "E2.7.6.0", {"start": v(33.02, -8.9) * mm, "end": v(45.72, -8.9) * mm});
            skLineSegment(sketch, "E2.7.6.1", {"start": v(33.02, -8.9) * mm, "end": v(33.02, -21.6) * mm});
            skLineSegment(sketch, "E2.7.6.2", {"start": v(33.02, -21.6) * mm, "end": v(45.72, -21.6) * mm});
            skLineSegment(sketch, "E2.7.6.3", {"start": v(45.72, -8.9) * mm, "end": v(45.72, -21.6) * mm});
            skLineSegment(sketch, "E2.7.7.0", {"start": v(33.02, -24.13) * mm, "end": v(45.72, -24.13) * mm});
            skLineSegment(sketch, "E2.7.7.1", {"start": v(33.02, -24.13) * mm, "end": v(33.02, -36.83) * mm});
            skLineSegment(sketch, "E2.7.7.2", {"start": v(33.02, -36.83) * mm, "end": v(45.72, -36.83) * mm});
            skLineSegment(sketch, "E2.7.7.3", {"start": v(45.72, -24.13) * mm, "end": v(45.72, -36.83) * mm});
            skLineSegment(sketch, "E2.7.8.0", {"start": v(33.02, -39.37) * mm, "end": v(45.72, -39.37) * mm});
            skLineSegment(sketch, "E2.7.8.1", {"start": v(33.02, -39.37) * mm, "end": v(33.02, -52.07) * mm});
            skLineSegment(sketch, "E2.7.8.2", {"start": v(33.02, -52.07) * mm, "end": v(45.72, -52.07) * mm});
            skLineSegment(sketch, "E2.7.8.3", {"start": v(45.72, -39.37) * mm, "end": v(45.72, -52.07) * mm});
            skLineSegment(sketch, "E2.7.9.0", {"start": v(33.02, -54.61) * mm, "end": v(45.72, -54.61) * mm});
            skLineSegment(sketch, "E2.7.9.1", {"start": v(33.02, -54.61) * mm, "end": v(33.02, -67.31) * mm});
            skLineSegment(sketch, "E2.7.9.2", {"start": v(33.02, -67.31) * mm, "end": v(45.72, -67.31) * mm});
            skLineSegment(sketch, "E2.7.9.3", {"start": v(45.72, -54.61) * mm, "end": v(45.72, -67.31) * mm});
            skLineSegment(sketch, "E2.8.0.0", {"start": v(48.26, 82.55) * mm, "end": v(60.96, 82.55) * mm});
            skLineSegment(sketch, "E2.8.0.1", {"start": v(48.26, 82.55) * mm, "end": v(48.26, 69.85) * mm});
            skLineSegment(sketch, "E2.8.0.2", {"start": v(48.26, 69.85) * mm, "end": v(60.96, 69.85) * mm});
            skLineSegment(sketch, "E2.8.0.3", {"start": v(60.96, 82.55) * mm, "end": v(60.96, 69.85) * mm});
            skLineSegment(sketch, "E2.8.1.0", {"start": v(48.26, 67.31) * mm, "end": v(60.96, 67.31) * mm});
            skLineSegment(sketch, "E2.8.1.1", {"start": v(48.26, 67.31) * mm, "end": v(48.26, 54.61) * mm});
            skLineSegment(sketch, "E2.8.1.2", {"start": v(48.26, 54.61) * mm, "end": v(60.96, 54.61) * mm});
            skLineSegment(sketch, "E2.8.1.3", {"start": v(60.96, 67.31) * mm, "end": v(60.96, 54.61) * mm});
            skLineSegment(sketch, "E2.8.2.0", {"start": v(48.26, 52.07) * mm, "end": v(60.96, 52.07) * mm});
            skLineSegment(sketch, "E2.8.2.1", {"start": v(48.26, 52.07) * mm, "end": v(48.26, 39.37) * mm});
            skLineSegment(sketch, "E2.8.2.2", {"start": v(48.26, 39.37) * mm, "end": v(60.96, 39.37) * mm});
            skLineSegment(sketch, "E2.8.2.3", {"start": v(60.96, 52.07) * mm, "end": v(60.96, 39.37) * mm});
            skLineSegment(sketch, "E2.8.3.0", {"start": v(48.26, 36.83) * mm, "end": v(60.96, 36.83) * mm});
            skLineSegment(sketch, "E2.8.3.1", {"start": v(48.26, 36.83) * mm, "end": v(48.26, 24.13) * mm});
            skLineSegment(sketch, "E2.8.3.2", {"start": v(48.26, 24.13) * mm, "end": v(60.96, 24.13) * mm});
            skLineSegment(sketch, "E2.8.3.3", {"start": v(60.96, 36.83) * mm, "end": v(60.96, 24.13) * mm});
            skLineSegment(sketch, "E2.8.4.0", {"start": v(48.26, 21.59) * mm, "end": v(60.96, 21.59) * mm});
            skLineSegment(sketch, "E2.8.4.1", {"start": v(48.26, 21.59) * mm, "end": v(48.26, 8.89) * mm});
            skLineSegment(sketch, "E2.8.4.2", {"start": v(48.26, 8.89) * mm, "end": v(60.96, 8.89) * mm});
            skLineSegment(sketch, "E2.8.4.3", {"start": v(60.96, 21.59) * mm, "end": v(60.96, 8.89) * mm});
            skLineSegment(sketch, "E2.8.5.0", {"start": v(48.26, 6.35) * mm, "end": v(60.96, 6.35) * mm});
            skLineSegment(sketch, "E2.8.5.1", {"start": v(48.26, 6.35) * mm, "end": v(48.26, -6.35) * mm});
            skLineSegment(sketch, "E2.8.5.2", {"start": v(48.26, -6.35) * mm, "end": v(60.96, -6.35) * mm});
            skLineSegment(sketch, "E2.8.5.3", {"start": v(60.96, 6.35) * mm, "end": v(60.96, -6.35) * mm});
            skLineSegment(sketch, "E2.8.6.0", {"start": v(48.26, -8.9) * mm, "end": v(60.96, -8.9) * mm});
            skLineSegment(sketch, "E2.8.6.1", {"start": v(48.26, -8.9) * mm, "end": v(48.26, -21.6) * mm});
            skLineSegment(sketch, "E2.8.6.2", {"start": v(48.26, -21.6) * mm, "end": v(60.96, -21.6) * mm});
            skLineSegment(sketch, "E2.8.6.3", {"start": v(60.96, -8.9) * mm, "end": v(60.96, -21.6) * mm});
            skLineSegment(sketch, "E2.8.7.0", {"start": v(48.26, -24.13) * mm, "end": v(60.96, -24.13) * mm});
            skLineSegment(sketch, "E2.8.7.1", {"start": v(48.26, -24.13) * mm, "end": v(48.26, -36.83) * mm});
            skLineSegment(sketch, "E2.8.7.2", {"start": v(48.26, -36.83) * mm, "end": v(60.96, -36.83) * mm});
            skLineSegment(sketch, "E2.8.7.3", {"start": v(60.96, -24.13) * mm, "end": v(60.96, -36.83) * mm});
            skLineSegment(sketch, "E2.8.8.0", {"start": v(48.26, -39.37) * mm, "end": v(60.96, -39.37) * mm});
            skLineSegment(sketch, "E2.8.8.1", {"start": v(48.26, -39.37) * mm, "end": v(48.26, -52.07) * mm});
            skLineSegment(sketch, "E2.8.8.2", {"start": v(48.26, -52.07) * mm, "end": v(60.96, -52.07) * mm});
            skLineSegment(sketch, "E2.8.8.3", {"start": v(60.96, -39.37) * mm, "end": v(60.96, -52.07) * mm});
            skLineSegment(sketch, "E2.8.9.0", {"start": v(48.26, -54.61) * mm, "end": v(60.96, -54.61) * mm});
            skLineSegment(sketch, "E2.8.9.1", {"start": v(48.26, -54.61) * mm, "end": v(48.26, -67.31) * mm});
            skLineSegment(sketch, "E2.8.9.2", {"start": v(48.26, -67.31) * mm, "end": v(60.96, -67.31) * mm});
            skLineSegment(sketch, "E2.8.9.3", {"start": v(60.96, -54.61) * mm, "end": v(60.96, -67.31) * mm});
            skLineSegment(sketch, "E2.9.0.0", {"start": v(63.5, 82.55) * mm, "end": v(76.2, 82.55) * mm});
            skLineSegment(sketch, "E2.9.0.1", {"start": v(63.5, 82.55) * mm, "end": v(63.5, 69.85) * mm});
            skLineSegment(sketch, "E2.9.0.2", {"start": v(63.5, 69.85) * mm, "end": v(76.2, 69.85) * mm});
            skLineSegment(sketch, "E2.9.0.3", {"start": v(76.2, 82.55) * mm, "end": v(76.2, 69.85) * mm});
            skLineSegment(sketch, "E2.9.1.0", {"start": v(63.5, 67.31) * mm, "end": v(76.2, 67.31) * mm});
            skLineSegment(sketch, "E2.9.1.1", {"start": v(63.5, 67.31) * mm, "end": v(63.5, 54.61) * mm});
            skLineSegment(sketch, "E2.9.1.2", {"start": v(63.5, 54.61) * mm, "end": v(76.2, 54.61) * mm});
            skLineSegment(sketch, "E2.9.1.3", {"start": v(76.2, 67.31) * mm, "end": v(76.2, 54.61) * mm});
            skLineSegment(sketch, "E2.9.2.0", {"start": v(63.5, 52.07) * mm, "end": v(76.2, 52.07) * mm});
            skLineSegment(sketch, "E2.9.2.1", {"start": v(63.5, 52.07) * mm, "end": v(63.5, 39.37) * mm});
            skLineSegment(sketch, "E2.9.2.2", {"start": v(63.5, 39.37) * mm, "end": v(76.2, 39.37) * mm});
            skLineSegment(sketch, "E2.9.2.3", {"start": v(76.2, 52.07) * mm, "end": v(76.2, 39.37) * mm});
            skLineSegment(sketch, "E2.9.3.0", {"start": v(63.5, 36.83) * mm, "end": v(76.2, 36.83) * mm});
            skLineSegment(sketch, "E2.9.3.1", {"start": v(63.5, 36.83) * mm, "end": v(63.5, 24.13) * mm});
            skLineSegment(sketch, "E2.9.3.2", {"start": v(63.5, 24.13) * mm, "end": v(76.2, 24.13) * mm});
            skLineSegment(sketch, "E2.9.3.3", {"start": v(76.2, 36.83) * mm, "end": v(76.2, 24.13) * mm});
            skLineSegment(sketch, "E2.9.4.0", {"start": v(63.5, 21.59) * mm, "end": v(76.2, 21.59) * mm});
            skLineSegment(sketch, "E2.9.4.1", {"start": v(63.5, 21.59) * mm, "end": v(63.5, 8.89) * mm});
            skLineSegment(sketch, "E2.9.4.2", {"start": v(63.5, 8.89) * mm, "end": v(76.2, 8.89) * mm});
            skLineSegment(sketch, "E2.9.4.3", {"start": v(76.2, 21.59) * mm, "end": v(76.2, 8.89) * mm});
            skLineSegment(sketch, "E2.9.5.0", {"start": v(63.5, 6.35) * mm, "end": v(76.2, 6.35) * mm});
            skLineSegment(sketch, "E2.9.5.1", {"start": v(63.5, 6.35) * mm, "end": v(63.5, -6.35) * mm});
            skLineSegment(sketch, "E2.9.5.2", {"start": v(63.5, -6.35) * mm, "end": v(76.2, -6.35) * mm});
            skLineSegment(sketch, "E2.9.5.3", {"start": v(76.2, 6.35) * mm, "end": v(76.2, -6.35) * mm});
            skLineSegment(sketch, "E2.9.6.0", {"start": v(63.5, -8.9) * mm, "end": v(76.2, -8.9) * mm});
            skLineSegment(sketch, "E2.9.6.1", {"start": v(63.5, -8.9) * mm, "end": v(63.5, -21.6) * mm});
            skLineSegment(sketch, "E2.9.6.2", {"start": v(63.5, -21.6) * mm, "end": v(76.2, -21.6) * mm});
            skLineSegment(sketch, "E2.9.6.3", {"start": v(76.2, -8.9) * mm, "end": v(76.2, -21.6) * mm});
            skLineSegment(sketch, "E2.9.7.0", {"start": v(63.5, -24.13) * mm, "end": v(76.2, -24.13) * mm});
            skLineSegment(sketch, "E2.9.7.1", {"start": v(63.5, -24.13) * mm, "end": v(63.5, -36.83) * mm});
            skLineSegment(sketch, "E2.9.7.2", {"start": v(63.5, -36.83) * mm, "end": v(76.2, -36.83) * mm});
            skLineSegment(sketch, "E2.9.7.3", {"start": v(76.2, -24.13) * mm, "end": v(76.2, -36.83) * mm});
            skLineSegment(sketch, "E2.9.8.0", {"start": v(63.5, -39.37) * mm, "end": v(76.2, -39.37) * mm});
            skLineSegment(sketch, "E2.9.8.1", {"start": v(63.5, -39.37) * mm, "end": v(63.5, -52.07) * mm});
            skLineSegment(sketch, "E2.9.8.2", {"start": v(63.5, -52.07) * mm, "end": v(76.2, -52.07) * mm});
            skLineSegment(sketch, "E2.9.8.3", {"start": v(76.2, -39.37) * mm, "end": v(76.2, -52.07) * mm});
            skLineSegment(sketch, "E2.9.9.0", {"start": v(63.5, -54.61) * mm, "end": v(76.2, -54.61) * mm});
            skLineSegment(sketch, "E2.9.9.1", {"start": v(63.5, -54.61) * mm, "end": v(63.5, -67.31) * mm});
            skLineSegment(sketch, "E2.9.9.2", {"start": v(63.5, -67.31) * mm, "end": v(76.2, -67.31) * mm});
            skLineSegment(sketch, "E2.9.9.3", {"start": v(76.2, -54.61) * mm, "end": v(76.2, -67.31) * mm});
            skLineSegment(sketch, "E2.direction1", {"start": v(-73.66, 82.55) * mm, "end": v(-58.42, 82.55) * mm, "construction": true});
            skLineSegment(sketch, "E2.direction2", {"start": v(-73.66, 82.55) * mm, "end": v(-73.66, 67.31) * mm, "construction": true});
            skLineSegment(sketch, "E3.bottom", {"start": v(-76.2, -67.31) * mm, "end": v(-88.9, -67.31) * mm});
            skLineSegment(sketch, "E3.top", {"start": v(-76.2, -54.61) * mm, "end": v(-88.9, -54.61) * mm});
            skLineSegment(sketch, "E3.left", {"start": v(-76.2, -67.31) * mm, "end": v(-76.2, -54.61) * mm});
            skLineSegment(sketch, "E3.right", {"start": v(-88.9, -67.31) * mm, "end": v(-88.9, -54.61) * mm});
            skLineSegment(sketch, "E4.0.1.0", {"start": v(-88.9, -52.07) * mm, "end": v(-88.9, -39.37) * mm});
            skLineSegment(sketch, "E4.0.1.1", {"start": v(-76.2, -52.07) * mm, "end": v(-76.2, -39.37) * mm});
            skLineSegment(sketch, "E4.0.1.2", {"start": v(-76.2, -39.37) * mm, "end": v(-88.9, -39.37) * mm});
            skLineSegment(sketch, "E4.0.1.3", {"start": v(-76.2, -52.07) * mm, "end": v(-88.9, -52.07) * mm});
            skLineSegment(sketch, "E4.0.2.0", {"start": v(-88.9, -36.83) * mm, "end": v(-88.9, -24.13) * mm});
            skLineSegment(sketch, "E4.0.2.1", {"start": v(-76.2, -36.83) * mm, "end": v(-76.2, -24.13) * mm});
            skLineSegment(sketch, "E4.0.2.2", {"start": v(-76.2, -24.13) * mm, "end": v(-88.9, -24.13) * mm});
            skLineSegment(sketch, "E4.0.2.3", {"start": v(-76.2, -36.83) * mm, "end": v(-88.9, -36.83) * mm});
            skLineSegment(sketch, "E4.0.3.0", {"start": v(-88.9, -21.6) * mm, "end": v(-88.9, -8.9) * mm});
            skLineSegment(sketch, "E4.0.3.1", {"start": v(-76.2, -21.6) * mm, "end": v(-76.2, -8.9) * mm});
            skLineSegment(sketch, "E4.0.3.2", {"start": v(-76.2, -8.9) * mm, "end": v(-88.9, -8.9) * mm});
            skLineSegment(sketch, "E4.0.3.3", {"start": v(-76.2, -21.6) * mm, "end": v(-88.9, -21.6) * mm});
            skLineSegment(sketch, "E4.0.4.0", {"start": v(-88.9, -6.35) * mm, "end": v(-88.9, 6.35) * mm});
            skLineSegment(sketch, "E4.0.4.1", {"start": v(-76.2, -6.35) * mm, "end": v(-76.2, 6.35) * mm});
            skLineSegment(sketch, "E4.0.4.2", {"start": v(-76.2, 6.35) * mm, "end": v(-88.9, 6.35) * mm});
            skLineSegment(sketch, "E4.0.4.3", {"start": v(-76.2, -6.35) * mm, "end": v(-88.9, -6.35) * mm});
            skLineSegment(sketch, "E4.0.5.0", {"start": v(-88.9, 8.89) * mm, "end": v(-88.9, 21.59) * mm});
            skLineSegment(sketch, "E4.0.5.1", {"start": v(-76.2, 8.89) * mm, "end": v(-76.2, 21.59) * mm});
            skLineSegment(sketch, "E4.0.5.2", {"start": v(-76.2, 21.59) * mm, "end": v(-88.9, 21.59) * mm});
            skLineSegment(sketch, "E4.0.5.3", {"start": v(-76.2, 8.89) * mm, "end": v(-88.9, 8.89) * mm});
            skLineSegment(sketch, "E4.0.6.0", {"start": v(-88.9, 24.13) * mm, "end": v(-88.9, 36.83) * mm});
            skLineSegment(sketch, "E4.0.6.1", {"start": v(-76.2, 24.13) * mm, "end": v(-76.2, 36.83) * mm});
            skLineSegment(sketch, "E4.0.6.2", {"start": v(-76.2, 36.83) * mm, "end": v(-88.9, 36.83) * mm});
            skLineSegment(sketch, "E4.0.6.3", {"start": v(-76.2, 24.13) * mm, "end": v(-88.9, 24.13) * mm});
            skLineSegment(sketch, "E4.0.7.0", {"start": v(-88.9, 39.37) * mm, "end": v(-88.9, 52.07) * mm});
            skLineSegment(sketch, "E4.0.7.1", {"start": v(-76.2, 39.37) * mm, "end": v(-76.2, 52.07) * mm});
            skLineSegment(sketch, "E4.0.7.2", {"start": v(-76.2, 52.07) * mm, "end": v(-88.9, 52.07) * mm});
            skLineSegment(sketch, "E4.0.7.3", {"start": v(-76.2, 39.37) * mm, "end": v(-88.9, 39.37) * mm});
            skLineSegment(sketch, "E4.0.8.0", {"start": v(-88.9, 54.61) * mm, "end": v(-88.9, 67.31) * mm});
            skLineSegment(sketch, "E4.0.8.1", {"start": v(-76.2, 54.61) * mm, "end": v(-76.2, 67.31) * mm});
            skLineSegment(sketch, "E4.0.8.2", {"start": v(-76.2, 67.31) * mm, "end": v(-88.9, 67.31) * mm});
            skLineSegment(sketch, "E4.0.8.3", {"start": v(-76.2, 54.61) * mm, "end": v(-88.9, 54.61) * mm});
            skLineSegment(sketch, "E4.1.2.0", {"start": v(-104.14, -36.83) * mm, "end": v(-104.14, -24.13) * mm});
            skLineSegment(sketch, "E4.1.2.1", {"start": v(-91.44, -36.83) * mm, "end": v(-91.44, -24.13) * mm});
            skLineSegment(sketch, "E4.1.2.2", {"start": v(-91.44, -24.13) * mm, "end": v(-104.14, -24.13) * mm});
            skLineSegment(sketch, "E4.1.2.3", {"start": v(-91.44, -36.83) * mm, "end": v(-104.14, -36.83) * mm});
            skLineSegment(sketch, "E4.1.3.0", {"start": v(-104.14, -21.6) * mm, "end": v(-104.14, -8.9) * mm});
            skLineSegment(sketch, "E4.1.3.1", {"start": v(-91.44, -21.6) * mm, "end": v(-91.44, -8.9) * mm});
            skLineSegment(sketch, "E4.1.3.2", {"start": v(-91.44, -8.9) * mm, "end": v(-104.14, -8.9) * mm});
            skLineSegment(sketch, "E4.1.3.3", {"start": v(-91.44, -21.6) * mm, "end": v(-104.14, -21.6) * mm});
            skLineSegment(sketch, "E4.1.4.0", {"start": v(-104.14, -6.35) * mm, "end": v(-104.14, 6.35) * mm});
            skLineSegment(sketch, "E4.1.4.1", {"start": v(-91.44, -6.35) * mm, "end": v(-91.44, 6.35) * mm});
            skLineSegment(sketch, "E4.1.4.2", {"start": v(-91.44, 6.35) * mm, "end": v(-104.14, 6.35) * mm});
            skLineSegment(sketch, "E4.1.4.3", {"start": v(-91.44, -6.35) * mm, "end": v(-104.14, -6.35) * mm});
            skLineSegment(sketch, "E4.1.5.0", {"start": v(-104.14, 8.89) * mm, "end": v(-104.14, 21.59) * mm});
            skLineSegment(sketch, "E4.1.5.1", {"start": v(-91.44, 8.89) * mm, "end": v(-91.44, 21.59) * mm});
            skLineSegment(sketch, "E4.1.5.2", {"start": v(-91.44, 21.59) * mm, "end": v(-104.14, 21.59) * mm});
            skLineSegment(sketch, "E4.1.5.3", {"start": v(-91.44, 8.89) * mm, "end": v(-104.14, 8.89) * mm});
            skLineSegment(sketch, "E4.1.6.0", {"start": v(-104.14, 24.13) * mm, "end": v(-104.14, 36.83) * mm});
            skLineSegment(sketch, "E4.1.6.1", {"start": v(-91.44, 24.13) * mm, "end": v(-91.44, 36.83) * mm});
            skLineSegment(sketch, "E4.1.6.2", {"start": v(-91.44, 36.83) * mm, "end": v(-104.14, 36.83) * mm});
            skLineSegment(sketch, "E4.1.6.3", {"start": v(-91.44, 24.13) * mm, "end": v(-104.14, 24.13) * mm});
            skLineSegment(sketch, "E4.direction2", {"start": v(-88.9, -67.31) * mm, "end": v(-88.9, -52.07) * mm, "construction": true});
            skLineSegment(sketch, "E5.bottom", {"start": v(79.26, -67.31) * mm, "end": v(91.96, -67.31) * mm});
            skLineSegment(sketch, "E5.top", {"start": v(79.26, -54.61) * mm, "end": v(91.96, -54.61) * mm});
            skLineSegment(sketch, "E5.left", {"start": v(79.26, -67.31) * mm, "end": v(79.26, -54.61) * mm});
            skLineSegment(sketch, "E5.right", {"start": v(91.96, -67.31) * mm, "end": v(91.96, -54.61) * mm});
            skLineSegment(sketch, "E6.0.1.0", {"start": v(79.26, -39.37) * mm, "end": v(91.96, -39.37) * mm});
            skLineSegment(sketch, "E6.0.1.1", {"start": v(91.96, -52.07) * mm, "end": v(91.96, -39.37) * mm});
            skLineSegment(sketch, "E6.0.1.2", {"start": v(79.26, -52.07) * mm, "end": v(91.96, -52.07) * mm});
            skLineSegment(sketch, "E6.0.1.3", {"start": v(79.26, -52.07) * mm, "end": v(79.26, -39.37) * mm});
            skLineSegment(sketch, "E6.0.2.0", {"start": v(79.26, -24.13) * mm, "end": v(91.96, -24.13) * mm});
            skLineSegment(sketch, "E6.0.2.1", {"start": v(91.96, -36.83) * mm, "end": v(91.96, -24.13) * mm});
            skLineSegment(sketch, "E6.0.2.2", {"start": v(79.26, -36.83) * mm, "end": v(91.96, -36.83) * mm});
            skLineSegment(sketch, "E6.0.2.3", {"start": v(79.26, -36.83) * mm, "end": v(79.26, -24.13) * mm});
            skLineSegment(sketch, "E6.0.3.0", {"start": v(79.26, -8.9) * mm, "end": v(91.96, -8.9) * mm});
            skLineSegment(sketch, "E6.0.3.1", {"start": v(91.96, -21.6) * mm, "end": v(91.96, -8.9) * mm});
            skLineSegment(sketch, "E6.0.3.2", {"start": v(79.26, -21.6) * mm, "end": v(91.96, -21.6) * mm});
            skLineSegment(sketch, "E6.0.3.3", {"start": v(79.26, -21.6) * mm, "end": v(79.26, -8.9) * mm});
            skLineSegment(sketch, "E6.0.4.0", {"start": v(79.26, 6.35) * mm, "end": v(91.96, 6.35) * mm});
            skLineSegment(sketch, "E6.0.4.1", {"start": v(91.96, -6.35) * mm, "end": v(91.96, 6.35) * mm});
            skLineSegment(sketch, "E6.0.4.2", {"start": v(79.26, -6.35) * mm, "end": v(91.96, -6.35) * mm});
            skLineSegment(sketch, "E6.0.4.3", {"start": v(79.26, -6.35) * mm, "end": v(79.26, 6.35) * mm});
            skLineSegment(sketch, "E6.0.5.0", {"start": v(79.26, 21.59) * mm, "end": v(91.96, 21.59) * mm});
            skLineSegment(sketch, "E6.0.5.1", {"start": v(91.96, 8.89) * mm, "end": v(91.96, 21.59) * mm});
            skLineSegment(sketch, "E6.0.5.2", {"start": v(79.26, 8.89) * mm, "end": v(91.96, 8.89) * mm});
            skLineSegment(sketch, "E6.0.5.3", {"start": v(79.26, 8.89) * mm, "end": v(79.26, 21.59) * mm});
            skLineSegment(sketch, "E6.0.6.0", {"start": v(79.26, 36.83) * mm, "end": v(91.96, 36.83) * mm});
            skLineSegment(sketch, "E6.0.6.1", {"start": v(91.96, 24.13) * mm, "end": v(91.96, 36.83) * mm});
            skLineSegment(sketch, "E6.0.6.2", {"start": v(79.26, 24.13) * mm, "end": v(91.96, 24.13) * mm});
            skLineSegment(sketch, "E6.0.6.3", {"start": v(79.26, 24.13) * mm, "end": v(79.26, 36.83) * mm});
            skLineSegment(sketch, "E6.0.7.0", {"start": v(79.26, 52.07) * mm, "end": v(91.96, 52.07) * mm});
            skLineSegment(sketch, "E6.0.7.1", {"start": v(91.96, 39.37) * mm, "end": v(91.96, 52.07) * mm});
            skLineSegment(sketch, "E6.0.7.2", {"start": v(79.26, 39.37) * mm, "end": v(91.96, 39.37) * mm});
            skLineSegment(sketch, "E6.0.7.3", {"start": v(79.26, 39.37) * mm, "end": v(79.26, 52.07) * mm});
            skLineSegment(sketch, "E6.0.8.0", {"start": v(79.26, 67.31) * mm, "end": v(91.96, 67.31) * mm});
            skLineSegment(sketch, "E6.0.8.1", {"start": v(91.96, 54.61) * mm, "end": v(91.96, 67.31) * mm});
            skLineSegment(sketch, "E6.0.8.2", {"start": v(79.26, 54.61) * mm, "end": v(91.96, 54.61) * mm});
            skLineSegment(sketch, "E6.0.8.3", {"start": v(79.26, 54.61) * mm, "end": v(79.26, 67.31) * mm});
            skLineSegment(sketch, "E6.1.2.0", {"start": v(94.5, -24.13) * mm, "end": v(107.2, -24.13) * mm});
            skLineSegment(sketch, "E6.1.2.1", {"start": v(107.2, -36.83) * mm, "end": v(107.2, -24.13) * mm});
            skLineSegment(sketch, "E6.1.2.2", {"start": v(94.5, -36.83) * mm, "end": v(107.2, -36.83) * mm});
            skLineSegment(sketch, "E6.1.2.3", {"start": v(94.5, -36.83) * mm, "end": v(94.5, -24.13) * mm});
            skLineSegment(sketch, "E6.1.3.0", {"start": v(94.5, -8.9) * mm, "end": v(107.2, -8.9) * mm});
            skLineSegment(sketch, "E6.1.3.1", {"start": v(107.2, -21.6) * mm, "end": v(107.2, -8.9) * mm});
            skLineSegment(sketch, "E6.1.3.2", {"start": v(94.5, -21.6) * mm, "end": v(107.2, -21.6) * mm});
            skLineSegment(sketch, "E6.1.3.3", {"start": v(94.5, -21.6) * mm, "end": v(94.5, -8.9) * mm});
            skLineSegment(sketch, "E6.1.4.0", {"start": v(94.5, 6.35) * mm, "end": v(107.2, 6.35) * mm});
            skLineSegment(sketch, "E6.1.4.1", {"start": v(107.2, -6.35) * mm, "end": v(107.2, 6.35) * mm});
            skLineSegment(sketch, "E6.1.4.2", {"start": v(94.5, -6.35) * mm, "end": v(107.2, -6.35) * mm});
            skLineSegment(sketch, "E6.1.4.3", {"start": v(94.5, -6.35) * mm, "end": v(94.5, 6.35) * mm});
            skLineSegment(sketch, "E6.1.5.0", {"start": v(94.5, 21.59) * mm, "end": v(107.2, 21.59) * mm});
            skLineSegment(sketch, "E6.1.5.1", {"start": v(107.2, 8.89) * mm, "end": v(107.2, 21.59) * mm});
            skLineSegment(sketch, "E6.1.5.2", {"start": v(94.5, 8.89) * mm, "end": v(107.2, 8.89) * mm});
            skLineSegment(sketch, "E6.1.5.3", {"start": v(94.5, 8.89) * mm, "end": v(94.5, 21.59) * mm});
            skLineSegment(sketch, "E6.1.6.0", {"start": v(94.5, 36.83) * mm, "end": v(107.2, 36.83) * mm});
            skLineSegment(sketch, "E6.1.6.1", {"start": v(107.2, 24.13) * mm, "end": v(107.2, 36.83) * mm});
            skLineSegment(sketch, "E6.1.6.2", {"start": v(94.5, 24.13) * mm, "end": v(107.2, 24.13) * mm});
            skLineSegment(sketch, "E6.1.6.3", {"start": v(94.5, 24.13) * mm, "end": v(94.5, 36.83) * mm});
            skLineSegment(sketch, "E6.direction1", {"start": v(79.26, -67.31) * mm, "end": v(94.5, -67.31) * mm, "construction": true});
            skLineSegment(sketch, "E6.direction2", {"start": v(79.26, -67.31) * mm, "end": v(79.26, -52.07) * mm, "construction": true});
            skLineSegment(sketch, "E7.bottom", {"start": v(-58.42, 85.1) * mm, "end": v(-45.72, 85.1) * mm});
            skLineSegment(sketch, "E7.top", {"start": v(-58.42, 97.8) * mm, "end": v(-45.72, 97.8) * mm});
            skLineSegment(sketch, "E7.left", {"start": v(-58.42, 85.1) * mm, "end": v(-58.42, 97.8) * mm});
            skLineSegment(sketch, "E7.right", {"start": v(-45.72, 85.1) * mm, "end": v(-45.72, 97.8) * mm});
            skLineSegment(sketch, "E8.1.0.0", {"start": v(-30.48, 85.1) * mm, "end": v(-30.48, 97.8) * mm});
            skLineSegment(sketch, "E8.1.0.1", {"start": v(-43.18, 85.1) * mm, "end": v(-30.48, 85.1) * mm});
            skLineSegment(sketch, "E8.1.0.2", {"start": v(-43.18, 97.8) * mm, "end": v(-30.48, 97.8) * mm});
            skLineSegment(sketch, "E8.1.0.3", {"start": v(-43.18, 85.1) * mm, "end": v(-43.18, 97.8) * mm});
            skLineSegment(sketch, "E8.2.0.0", {"start": v(-15.24, 85.1) * mm, "end": v(-15.24, 97.8) * mm});
            skLineSegment(sketch, "E8.2.0.1", {"start": v(-27.94, 85.1) * mm, "end": v(-15.24, 85.1) * mm});
            skLineSegment(sketch, "E8.2.0.2", {"start": v(-27.94, 97.8) * mm, "end": v(-15.24, 97.8) * mm});
            skLineSegment(sketch, "E8.2.0.3", {"start": v(-27.94, 85.1) * mm, "end": v(-27.94, 97.8) * mm});
            skLineSegment(sketch, "E8.3.0.0", {"start": v(0, 85.1) * mm, "end": v(0, 97.8) * mm});
            skLineSegment(sketch, "E8.3.0.1", {"start": v(-12.7, 85.1) * mm, "end": v(0, 85.1) * mm});
            skLineSegment(sketch, "E8.3.0.2", {"start": v(-12.7, 97.8) * mm, "end": v(0, 97.8) * mm});
            skLineSegment(sketch, "E8.3.0.3", {"start": v(-12.7, 85.1) * mm, "end": v(-12.7, 97.8) * mm});
            skLineSegment(sketch, "E8.4.0.0", {"start": v(15.24, 85.1) * mm, "end": v(15.24, 97.8) * mm});
            skLineSegment(sketch, "E8.4.0.1", {"start": v(2.54, 85.1) * mm, "end": v(15.24, 85.1) * mm});
            skLineSegment(sketch, "E8.4.0.2", {"start": v(2.54, 97.8) * mm, "end": v(15.24, 97.8) * mm});
            skLineSegment(sketch, "E8.4.0.3", {"start": v(2.54, 85.1) * mm, "end": v(2.54, 97.8) * mm});
            skLineSegment(sketch, "E8.5.0.0", {"start": v(30.48, 85.1) * mm, "end": v(30.48, 97.8) * mm});
            skLineSegment(sketch, "E8.5.0.1", {"start": v(17.78, 85.1) * mm, "end": v(30.48, 85.1) * mm});
            skLineSegment(sketch, "E8.5.0.2", {"start": v(17.78, 97.8) * mm, "end": v(30.48, 97.8) * mm});
            skLineSegment(sketch, "E8.5.0.3", {"start": v(17.78, 85.1) * mm, "end": v(17.78, 97.8) * mm});
            skLineSegment(sketch, "E8.6.0.0", {"start": v(45.72, 85.1) * mm, "end": v(45.72, 97.8) * mm});
            skLineSegment(sketch, "E8.6.0.1", {"start": v(33.02, 85.1) * mm, "end": v(45.72, 85.1) * mm});
            skLineSegment(sketch, "E8.6.0.2", {"start": v(33.02, 97.8) * mm, "end": v(45.72, 97.8) * mm});
            skLineSegment(sketch, "E8.6.0.3", {"start": v(33.02, 85.1) * mm, "end": v(33.02, 97.8) * mm});
            skLineSegment(sketch, "E8.direction1", {"start": v(-58.42, 85.1) * mm, "end": v(-43.18, 85.1) * mm, "construction": true});
            skLineSegment(sketch, "E9.1.0.0", {"start": v(-60.96, -69.85) * mm, "end": v(-73.66, -69.85) * mm});
            skLineSegment(sketch, "E9.1.0.1", {"start": v(-73.66, -69.85) * mm, "end": v(-73.66, -82.55) * mm});
            skLineSegment(sketch, "E9.1.0.2", {"start": v(-60.96, -69.85) * mm, "end": v(-60.96, -82.55) * mm});
            skLineSegment(sketch, "E9.1.0.3", {"start": v(-60.96, -82.55) * mm, "end": v(-73.66, -82.55) * mm});
            skLineSegment(sketch, "E9.2.0.0", {"start": v(-45.72, -69.85) * mm, "end": v(-58.42, -69.85) * mm});
            skLineSegment(sketch, "E9.2.0.1", {"start": v(-58.42, -69.85) * mm, "end": v(-58.42, -82.55) * mm});
            skLineSegment(sketch, "E9.2.0.2", {"start": v(-45.72, -69.85) * mm, "end": v(-45.72, -82.55) * mm});
            skLineSegment(sketch, "E9.2.0.3", {"start": v(-45.72, -82.55) * mm, "end": v(-58.42, -82.55) * mm});
            skLineSegment(sketch, "E9.3.0.0", {"start": v(-30.48, -69.85) * mm, "end": v(-43.18, -69.85) * mm});
            skLineSegment(sketch, "E9.3.0.1", {"start": v(-43.18, -69.85) * mm, "end": v(-43.18, -82.55) * mm});
            skLineSegment(sketch, "E9.3.0.2", {"start": v(-30.48, -69.85) * mm, "end": v(-30.48, -82.55) * mm});
            skLineSegment(sketch, "E9.3.0.3", {"start": v(-30.48, -82.55) * mm, "end": v(-43.18, -82.55) * mm});
            skLineSegment(sketch, "E9.3.1.0", {"start": v(-30.48, -85.1) * mm, "end": v(-43.18, -85.1) * mm});
            skLineSegment(sketch, "E9.3.1.1", {"start": v(-43.18, -85.1) * mm, "end": v(-43.18, -97.8) * mm});
            skLineSegment(sketch, "E9.3.1.2", {"start": v(-30.48, -85.1) * mm, "end": v(-30.48, -97.8) * mm});
            skLineSegment(sketch, "E9.3.1.3", {"start": v(-30.48, -97.8) * mm, "end": v(-43.18, -97.8) * mm});
            skLineSegment(sketch, "E9.4.0.0", {"start": v(-15.24, -69.85) * mm, "end": v(-27.94, -69.85) * mm});
            skLineSegment(sketch, "E9.4.0.1", {"start": v(-27.94, -69.85) * mm, "end": v(-27.94, -82.55) * mm});
            skLineSegment(sketch, "E9.4.0.2", {"start": v(-15.24, -69.85) * mm, "end": v(-15.24, -82.55) * mm});
            skLineSegment(sketch, "E9.4.0.3", {"start": v(-15.24, -82.55) * mm, "end": v(-27.94, -82.55) * mm});
            skLineSegment(sketch, "E9.4.1.0", {"start": v(-15.24, -85.1) * mm, "end": v(-27.94, -85.1) * mm});
            skLineSegment(sketch, "E9.4.1.1", {"start": v(-27.94, -85.1) * mm, "end": v(-27.94, -97.8) * mm});
            skLineSegment(sketch, "E9.4.1.2", {"start": v(-15.24, -85.1) * mm, "end": v(-15.24, -97.8) * mm});
            skLineSegment(sketch, "E9.4.1.3", {"start": v(-15.24, -97.8) * mm, "end": v(-27.94, -97.8) * mm});
            skLineSegment(sketch, "E9.5.0.0", {"start": v(0, -69.85) * mm, "end": v(-12.7, -69.85) * mm});
            skLineSegment(sketch, "E9.5.0.1", {"start": v(-12.7, -69.85) * mm, "end": v(-12.7, -82.55) * mm});
            skLineSegment(sketch, "E9.5.0.2", {"start": v(0, -69.85) * mm, "end": v(0, -82.55) * mm});
            skLineSegment(sketch, "E9.5.0.3", {"start": v(0, -82.55) * mm, "end": v(-12.7, -82.55) * mm});
            skLineSegment(sketch, "E9.5.1.0", {"start": v(0, -85.1) * mm, "end": v(-12.7, -85.1) * mm});
            skLineSegment(sketch, "E9.5.1.1", {"start": v(-12.7, -85.1) * mm, "end": v(-12.7, -97.8) * mm});
            skLineSegment(sketch, "E9.5.1.2", {"start": v(0, -85.1) * mm, "end": v(0, -97.8) * mm});
            skLineSegment(sketch, "E9.5.1.3", {"start": v(0, -97.8) * mm, "end": v(-12.7, -97.8) * mm});
            skLineSegment(sketch, "E9.6.0.0", {"start": v(15.24, -69.85) * mm, "end": v(2.54, -69.85) * mm});
            skLineSegment(sketch, "E9.6.0.1", {"start": v(2.54, -69.85) * mm, "end": v(2.54, -82.55) * mm});
            skLineSegment(sketch, "E9.6.0.2", {"start": v(15.24, -69.85) * mm, "end": v(15.24, -82.55) * mm});
            skLineSegment(sketch, "E9.6.0.3", {"start": v(15.24, -82.55) * mm, "end": v(2.54, -82.55) * mm});
            skLineSegment(sketch, "E9.6.1.0", {"start": v(15.24, -85.1) * mm, "end": v(2.54, -85.1) * mm});
            skLineSegment(sketch, "E9.6.1.1", {"start": v(2.54, -85.1) * mm, "end": v(2.54, -97.8) * mm});
            skLineSegment(sketch, "E9.6.1.2", {"start": v(15.24, -85.1) * mm, "end": v(15.24, -97.8) * mm});
            skLineSegment(sketch, "E9.6.1.3", {"start": v(15.24, -97.8) * mm, "end": v(2.54, -97.8) * mm});
            skLineSegment(sketch, "E9.7.0.0", {"start": v(30.48, -69.85) * mm, "end": v(17.78, -69.85) * mm});
            skLineSegment(sketch, "E9.7.0.1", {"start": v(17.78, -69.85) * mm, "end": v(17.78, -82.55) * mm});
            skLineSegment(sketch, "E9.7.0.2", {"start": v(30.48, -69.85) * mm, "end": v(30.48, -82.55) * mm});
            skLineSegment(sketch, "E9.7.0.3", {"start": v(30.48, -82.55) * mm, "end": v(17.78, -82.55) * mm});
            skLineSegment(sketch, "E9.7.1.0", {"start": v(30.48, -85.1) * mm, "end": v(17.78, -85.1) * mm});
            skLineSegment(sketch, "E9.7.1.1", {"start": v(17.78, -85.1) * mm, "end": v(17.78, -97.8) * mm});
            skLineSegment(sketch, "E9.7.1.2", {"start": v(30.48, -85.1) * mm, "end": v(30.48, -97.8) * mm});
            skLineSegment(sketch, "E9.7.1.3", {"start": v(30.48, -97.8) * mm, "end": v(17.78, -97.8) * mm});
            skLineSegment(sketch, "E9.8.0.0", {"start": v(45.72, -69.85) * mm, "end": v(33.02, -69.85) * mm});
            skLineSegment(sketch, "E9.8.0.1", {"start": v(33.02, -69.85) * mm, "end": v(33.02, -82.55) * mm});
            skLineSegment(sketch, "E9.8.0.2", {"start": v(45.72, -69.85) * mm, "end": v(45.72, -82.55) * mm});
            skLineSegment(sketch, "E9.8.0.3", {"start": v(45.72, -82.55) * mm, "end": v(33.02, -82.55) * mm});
            skLineSegment(sketch, "E9.8.1.0", {"start": v(45.72, -85.1) * mm, "end": v(33.02, -85.1) * mm});
            skLineSegment(sketch, "E9.8.1.1", {"start": v(33.02, -85.1) * mm, "end": v(33.02, -97.8) * mm});
            skLineSegment(sketch, "E9.8.1.2", {"start": v(45.72, -85.1) * mm, "end": v(45.72, -97.8) * mm});
            skLineSegment(sketch, "E9.8.1.3", {"start": v(45.72, -97.8) * mm, "end": v(33.02, -97.8) * mm});
            skLineSegment(sketch, "E9.9.0.0", {"start": v(60.96, -69.85) * mm, "end": v(48.26, -69.85) * mm});
            skLineSegment(sketch, "E9.9.0.1", {"start": v(48.26, -69.85) * mm, "end": v(48.26, -82.55) * mm});
            skLineSegment(sketch, "E9.9.0.2", {"start": v(60.96, -69.85) * mm, "end": v(60.96, -82.55) * mm});
            skLineSegment(sketch, "E9.9.0.3", {"start": v(60.96, -82.55) * mm, "end": v(48.26, -82.55) * mm});
            skLineSegment(sketch, "E9.10.0.0", {"start": v(76.2, -69.85) * mm, "end": v(63.5, -69.85) * mm});
            skLineSegment(sketch, "E9.10.0.1", {"start": v(63.5, -69.85) * mm, "end": v(63.5, -82.55) * mm});
            skLineSegment(sketch, "E9.10.0.2", {"start": v(76.2, -69.85) * mm, "end": v(76.2, -82.55) * mm});
            skLineSegment(sketch, "E9.10.0.3", {"start": v(76.2, -82.55) * mm, "end": v(63.5, -82.55) * mm});
            skLineSegment(sketch, "E9.direction1", {"start": v(-88.9, -82.55) * mm, "end": v(-73.66, -82.55) * mm, "construction": true});
            skLineSegment(sketch, "E9.direction2", {"start": v(-88.9, -82.55) * mm, "end": v(-88.9, -97.8) * mm, "construction": true});
            skSolve(sketch);
        }
        {
            var Q0;
            Q0 = qSketchRegion(id + "F2", true);
            extrude(context, id + "F3", {"entities" : qUnion([Q0]), "operationType" : NewBodyOperationType.REMOVE, "oppositeDirection" : true, "depth" : 50.8 * mm});
        }
    });
